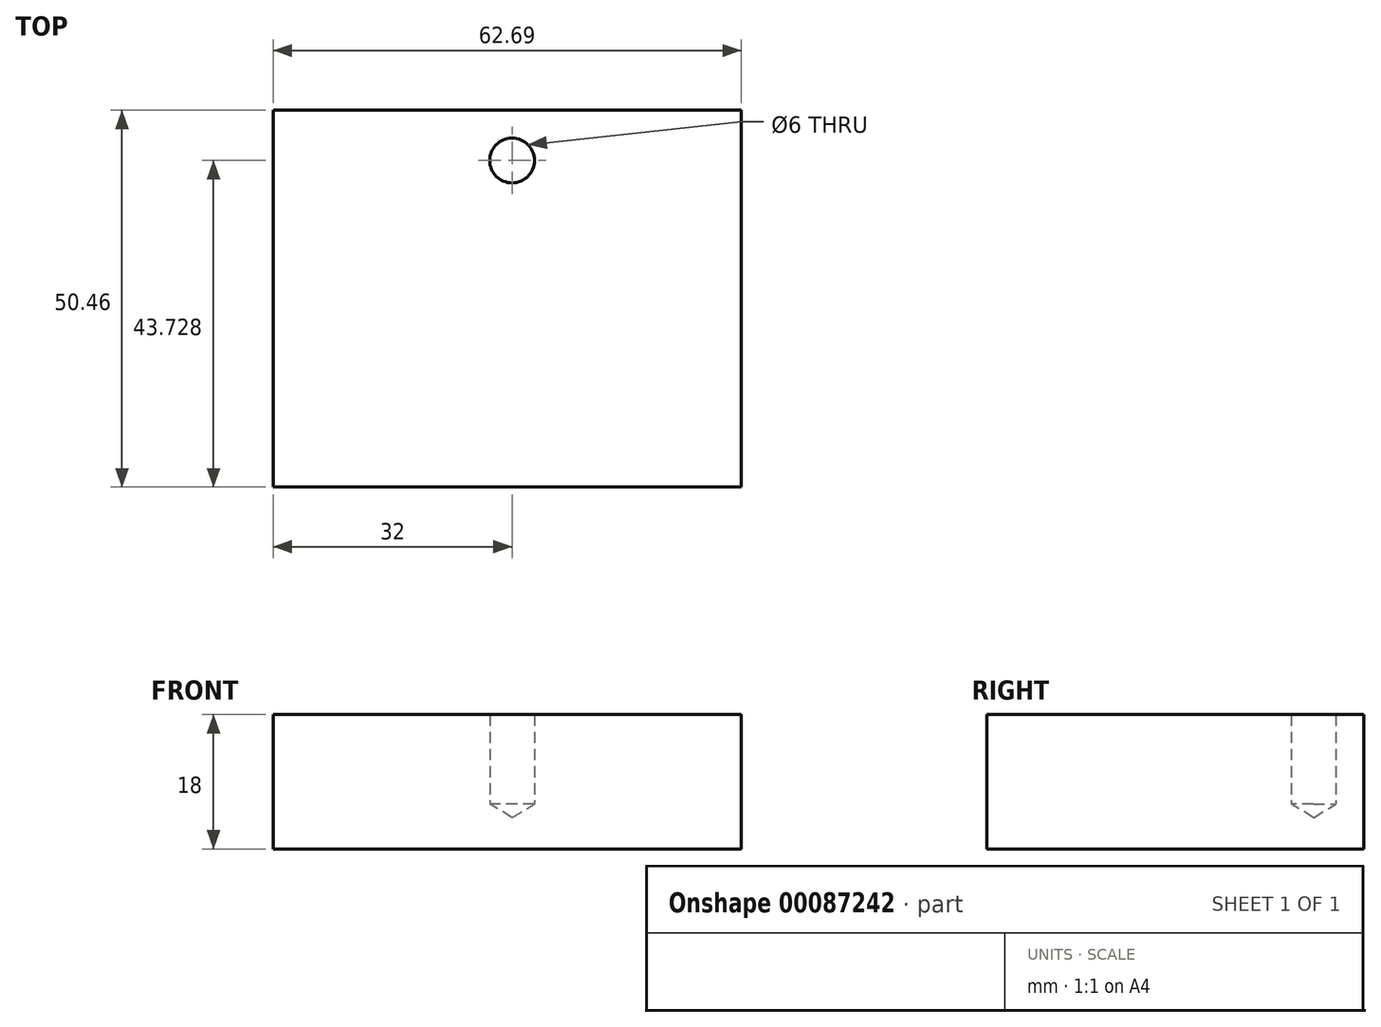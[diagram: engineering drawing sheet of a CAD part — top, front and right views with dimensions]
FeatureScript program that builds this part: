
annotation { "Feature Type Name" : "Feature", "Feature Type Description" : "" }
export const myFeature = defineFeature(function(context is Context, id is Id, definition is map)
    precondition{}
    {
        {
            var Q0;
            Q0=qCreatedBy(makeId("Top.planeOp"),FACE);
            var sketch = newSketch(context, id + "F0", { "sketchPlane" : qUnion([Q0])});
            skLineSegment(sketch, "E0.bottom", {"start": v(-32, 23.7) * mm, "end": v(30.7, 23.7) * mm});
            skLineSegment(sketch, "E0.top", {"start": v(-32, -26.76) * mm, "end": v(30.7, -26.76) * mm});
            skLineSegment(sketch, "E0.left", {"start": v(-32, 23.7) * mm, "end": v(-32, -26.76) * mm});
            skLineSegment(sketch, "E0.right", {"start": v(30.7, 23.7) * mm, "end": v(30.7, -26.76) * mm});
            skSolve(sketch);
        }
        {
            var Q0;
            Q0 = qSketchRegion(id + "F0", true);
            extrude(context, id + "F1", {"entities" : qUnion([Q0]), "depth" : 18 * mm});
        }
        {
            var Q0;
            Q0=makeQuery(id+"F1.opExtrude","CAP_FACE",FACE,{"disambiguationData":[OSD([sQuery(id+"F0.wireOp",EDGE,"E0.bottom"),sQuery(id+"F0.wireOp",EDGE,"E0.top"),sQuery(id+"F0.wireOp",EDGE,"E0.left"),sQuery(id+"F0.wireOp",EDGE,"E0.right")])],"isStart":false});
            var sketch = newSketch(context, id + "F2", { "sketchPlane" : qUnion([Q0])});
            skPoint(sketch, "E1", {"position": v(0, 16.97) * mm});
            skSolve(sketch);
        }
        {
            var Q0;
            Q0=sQuery(id+"F2.wireOp",VERTEX,"E1");
            var Q1;
            Q1=makeQuery(id+"F1.opExtrude","SWEPT_BODY",BODY,{"disambiguationData":[OSD([sQuery(id+"F0.wireOp",EDGE,"E0.bottom"),sQuery(id+"F0.wireOp",EDGE,"E0.top"),sQuery(id+"F0.wireOp",EDGE,"E0.left"),sQuery(id+"F0.wireOp",EDGE,"E0.right")])]});
            hole(context, id + "F3", {"style" : HoleStyle.SIMPLE, "endStyle" : HoleEndStyle.BLIND, "holeDiameter" : 6 * mm, "holeDepth" : 12 * mm, "locations" : qUnion([Q0]), "scope" : qUnion([Q1])});
        }
    });
